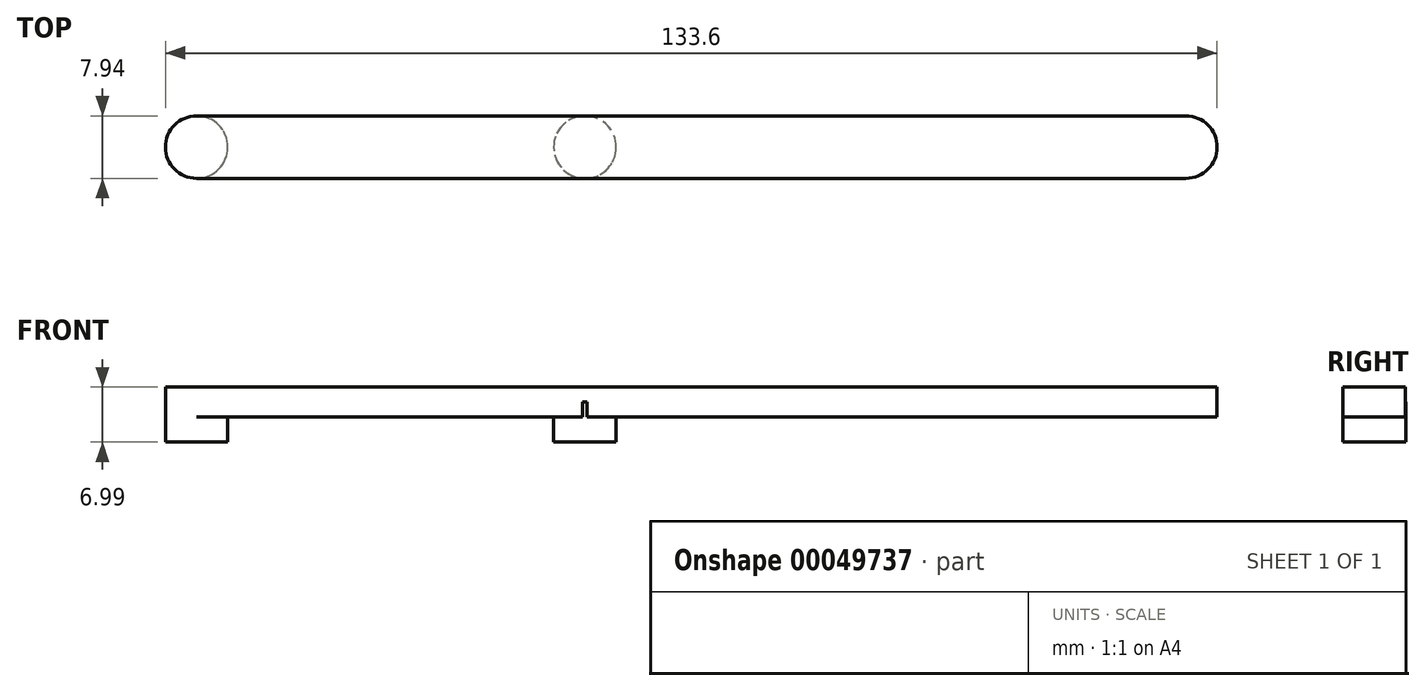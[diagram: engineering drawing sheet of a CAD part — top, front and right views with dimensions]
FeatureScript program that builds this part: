
annotation { "Feature Type Name" : "Feature", "Feature Type Description" : "" }
export const myFeature = defineFeature(function(context is Context, id is Id, definition is map)
    precondition{}
    {
        {
            var Q0;
            Q0=qCreatedBy(makeId("Top.planeOp"),FACE);
            var sketch = newSketch(context, id + "F0", { "sketchPlane" : qUnion([Q0])});
            skLineSegment(sketch, "E0.rect.bottom", {"start": v(-62.83, 3.96) * mm, "end": v(62.83, 3.96) * mm});
            skLineSegment(sketch, "E0.rect.top", {"start": v(-62.83, -3.96) * mm, "end": v(62.83, -3.96) * mm});
            skLineSegment(sketch, "E0.rect.left", {"start": v(-62.83, 3.96) * mm, "end": v(-62.83, -3.96) * mm});
            skLineSegment(sketch, "E0.rect.right", {"start": v(62.83, 3.96) * mm, "end": v(62.83, -3.96) * mm});
            skPoint(sketch, "E0.rect.middle", {"position": v(0, 0) * mm});
            skCircle(sketch, "E1", {"center": v(-62.83, 0) * mm, "radius": 3.96 * mm});
            skCircle(sketch, "E2", {"center": v(62.83, 0) * mm, "radius": 3.96 * mm});
            skSolve(sketch);
        }
        {
            var Q0;
            {var subQ1=sQuery(id+"F0.wireOp",EDGE,"E0.rect.left");Q0=makeQuery(id+"F0.imprint","IMPRINT",FACE,{"disambiguationData":[TD([[makeQuery(id+"F0.imprint","IMPRINT",EDGE,{"derivedFrom":subQ1}),-1.0]])]});}
            var Q1;
            {var subQ1=sQuery(id+"F0.wireOp",EDGE,"E0.rect.left");Q1=makeQuery(id+"F0.imprint","IMPRINT",FACE,{"disambiguationData":[TD([[makeQuery(id+"F0.imprint","IMPRINT",EDGE,{"derivedFrom":subQ1}),1.0]])]});}
            var Q2;
            {var subQ3=sQuery(id+"F0.wireOp",EDGE,"E0.rect.bottom");Q2=makeQuery(id+"F0.imprint","IMPRINT",FACE,{"disambiguationData":[TD([[makeQuery(id+"F0.imprint","IMPRINT",EDGE,{"derivedFrom":subQ3}),-1.0]])]});}
            var Q3;
            {var subQ1=sQuery(id+"F0.wireOp",EDGE,"E0.rect.right");Q3=makeQuery(id+"F0.imprint","IMPRINT",FACE,{"disambiguationData":[TD([[makeQuery(id+"F0.imprint","IMPRINT",EDGE,{"derivedFrom":subQ1}),-1.0]])]});}
            var Q4;
            {var subQ1=sQuery(id+"F0.wireOp",EDGE,"E0.rect.right");Q4=makeQuery(id+"F0.imprint","IMPRINT",FACE,{"disambiguationData":[TD([[makeQuery(id+"F0.imprint","IMPRINT",EDGE,{"derivedFrom":subQ1}),1.0]])]});}
            extrude(context, id + "F1", {"entities" : qUnion([Q0, Q1, Q2, Q3, Q4]), "depth" : 3.8 * mm, "symmetric" : true});
        }
        {
            var Q0;
            Q0=qCreatedBy(makeId("Top.planeOp"),FACE);
            var sketch = newSketch(context, id + "F2", { "sketchPlane" : qUnion([Q0])});
            skCircle(sketch, "E3", {"center": v(-13.5, 0) * mm, "radius": 3.97 * mm});
            skSolve(sketch);
        }
        {
            var Q0;
            Q0=makeQuery(id+"F2.imprint","IMPRINT",FACE,{"disambiguationData":[TD([[makeQuery(id+"F2.imprint","IMPRINT",EDGE,{"derivedFrom":sQuery(id+"F2.wireOp",EDGE,"E3")}),1.0]])]});
            var Q1;
            {var subQ1=sQuery(id+"F0.wireOp",EDGE,"E0.rect.left");Q1=makeQuery(id+"F0.imprint","IMPRINT",FACE,{"disambiguationData":[TD([[makeQuery(id+"F0.imprint","IMPRINT",EDGE,{"derivedFrom":subQ1}),1.0]])]});}
            var Q2;
            {var subQ1=sQuery(id+"F0.wireOp",EDGE,"E0.rect.left");Q2=makeQuery(id+"F0.imprint","IMPRINT",FACE,{"disambiguationData":[TD([[makeQuery(id+"F0.imprint","IMPRINT",EDGE,{"derivedFrom":subQ1}),-1.0]])]});}
            extrude(context, id + "F3", {"entities" : qUnion([Q0, Q1, Q2]), "operationType" : NewBodyOperationType.ADD, "oppositeDirection" : true, "depth" : 5.08 * mm});
        }
    });
